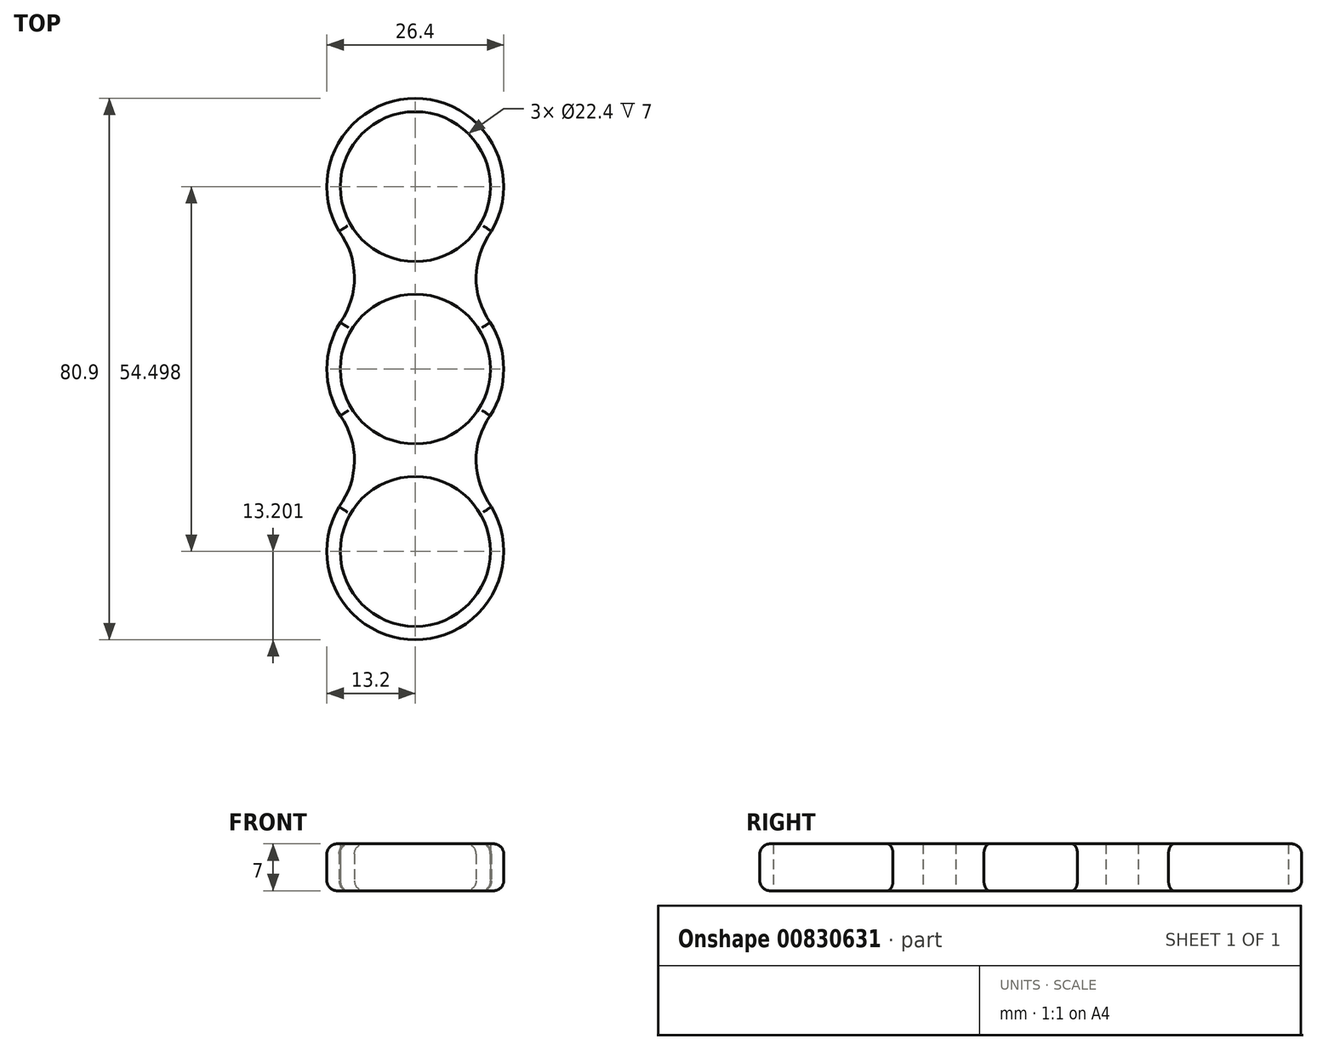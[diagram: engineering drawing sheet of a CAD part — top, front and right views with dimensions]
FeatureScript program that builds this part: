
annotation { "Feature Type Name" : "Feature", "Feature Type Description" : "" }
export const myFeature = defineFeature(function(context is Context, id is Id, definition is map)
    precondition{}
    {
        {
            var Q0;
            Q0=qCreatedBy(makeId("Top.planeOp"),FACE);
            var sketch = newSketch(context, id + "F0", { "sketchPlane" : qUnion([Q0])});
            skCircle(sketch, "E0", {"center": v(0, 0) * mm, "radius": 11.2 * mm});
            skArc(sketch, "E1", {"start": v(-10.8, 7.58) * mm, "mid": v(-13.2, 0) * mm, "end": v(-10.8, -7.58) * mm});
            skCircle(sketch, "E2", {"center": v(0, 27.25) * mm, "radius": 11.2 * mm});
            skArc(sketch, "E3", {"start": v(10.63, 19.42) * mm, "mid": v(0, 40.45) * mm, "end": v(-10.63, 19.42) * mm});
            skCircle(sketch, "E4.1.0", {"center": v(0, -27.25) * mm, "radius": 11.2 * mm});
            skArc(sketch, "E4.1.1", {"start": v(-10.63, -19.42) * mm, "mid": v(0, -40.45) * mm, "end": v(10.63, -19.42) * mm});
            skArc(sketch, "E5", {"start": v(11.38, 20.57) * mm, "mid": v(9.08, 13.8) * mm, "end": v(11.2, 6.99) * mm});
            skArc(sketch, "E6.MirrorCS", {"start": v(-11.38, 20.57) * mm, "mid": v(-9.08, 13.8) * mm, "end": v(-11.2, 6.99) * mm});
            skArc(sketch, "E7.MirrorCS", {"start": v(-11.38, -20.57) * mm, "mid": v(-9.08, -13.8) * mm, "end": v(-11.2, -6.99) * mm});
            skArc(sketch, "E8.MirrorCS", {"start": v(11.38, -20.57) * mm, "mid": v(9.08, -13.8) * mm, "end": v(11.2, -6.99) * mm});
            skArc(sketch, "E9.trimOffspring", {"start": v(10.8, -7.58) * mm, "mid": v(13.2, 0) * mm, "end": v(10.8, 7.58) * mm});
            skSolve(sketch);
        }
        {
            var Q0;
            Q0=makeQuery(id+"F0.imprint","IMPRINT",FACE,{"disambiguationData":[TD([[makeQuery(id+"F0.imprint","IMPRINT",EDGE,{"derivedFrom":sQuery(id+"F0.wireOp",EDGE,"E0")}),-1.0]])]});
            extrude(context, id + "F1", {"entities" : qUnion([Q0]), "depth" : 7 * mm, "offsetDistance" : 25 * mm});
        }
        {
            var Q0;
            Q0=makeQuery(id+"F1.opExtrude","CAP_EDGE",EDGE,{"disambiguationData":[OSD([sQuery(id+"F0.wireOp",EDGE,"E4.1.1")])],"isStart":false});
            var Q1;
            Q1=makeQuery(id+"F1.opExtrude","CAP_EDGE",EDGE,{"disambiguationData":[OSD([sQuery(id+"F0.wireOp",EDGE,"E8.MirrorCS")])],"isStart":false});
            var Q2;
            Q2=makeQuery(id+"F1.opExtrude","CAP_EDGE",EDGE,{"disambiguationData":[OSD([sQuery(id+"F0.wireOp",EDGE,"E9.trimOffspring")])],"isStart":false});
            var Q3;
            Q3=makeQuery(id+"F1.opExtrude","CAP_EDGE",EDGE,{"disambiguationData":[OSD([sQuery(id+"F0.wireOp",EDGE,"E5")])],"isStart":false});
            var Q4;
            Q4=makeQuery(id+"F1.opExtrude","CAP_EDGE",EDGE,{"disambiguationData":[OSD([sQuery(id+"F0.wireOp",EDGE,"E3")])],"isStart":false});
            var Q5;
            Q5=makeQuery(id+"F1.opExtrude","CAP_EDGE",EDGE,{"disambiguationData":[OSD([sQuery(id+"F0.wireOp",EDGE,"E6.MirrorCS")])],"isStart":false});
            var Q6;
            Q6=makeQuery(id+"F1.opExtrude","CAP_EDGE",EDGE,{"disambiguationData":[OSD([sQuery(id+"F0.wireOp",EDGE,"E1")])],"isStart":false});
            var Q7;
            Q7=makeQuery(id+"F1.opExtrude","CAP_EDGE",EDGE,{"disambiguationData":[OSD([sQuery(id+"F0.wireOp",EDGE,"E7.MirrorCS")])],"isStart":false});
            fillet(context, id + "F2", {"entities" : qUnion([Q0, Q1, Q2, Q3, Q4, Q5, Q6, Q7]), "radius" : 1.5 * mm, "tangentPropagation" : true, "allowEdgeOverflow" : false});
        }
        {
            var Q0;
            Q0=makeQuery(id+"F1.opExtrude","CAP_EDGE",EDGE,{"disambiguationData":[OSD([sQuery(id+"F0.wireOp",EDGE,"E4.1.1")])],"isStart":true});
            var Q1;
            Q1=makeQuery(id+"F1.opExtrude","CAP_EDGE",EDGE,{"disambiguationData":[OSD([sQuery(id+"F0.wireOp",EDGE,"E7.MirrorCS")])],"isStart":true});
            var Q2;
            Q2=makeQuery(id+"F1.opExtrude","CAP_EDGE",EDGE,{"disambiguationData":[OSD([sQuery(id+"F0.wireOp",EDGE,"E1")])],"isStart":true});
            var Q3;
            Q3=makeQuery(id+"F1.opExtrude","CAP_EDGE",EDGE,{"disambiguationData":[OSD([sQuery(id+"F0.wireOp",EDGE,"E6.MirrorCS")])],"isStart":true});
            var Q4;
            Q4=makeQuery(id+"F1.opExtrude","CAP_EDGE",EDGE,{"disambiguationData":[OSD([sQuery(id+"F0.wireOp",EDGE,"E3")])],"isStart":true});
            var Q5;
            Q5=makeQuery(id+"F1.opExtrude","CAP_EDGE",EDGE,{"disambiguationData":[OSD([sQuery(id+"F0.wireOp",EDGE,"E5")])],"isStart":true});
            var Q6;
            Q6=makeQuery(id+"F1.opExtrude","CAP_EDGE",EDGE,{"disambiguationData":[OSD([sQuery(id+"F0.wireOp",EDGE,"E9.trimOffspring")])],"isStart":true});
            var Q7;
            Q7=makeQuery(id+"F1.opExtrude","CAP_EDGE",EDGE,{"disambiguationData":[OSD([sQuery(id+"F0.wireOp",EDGE,"E8.MirrorCS")])],"isStart":true});
            fillet(context, id + "F3", {"entities" : qUnion([Q0, Q1, Q2, Q3, Q4, Q5, Q6, Q7]), "radius" : 1.5 * mm, "tangentPropagation" : true, "allowEdgeOverflow" : false});
        }
    });
